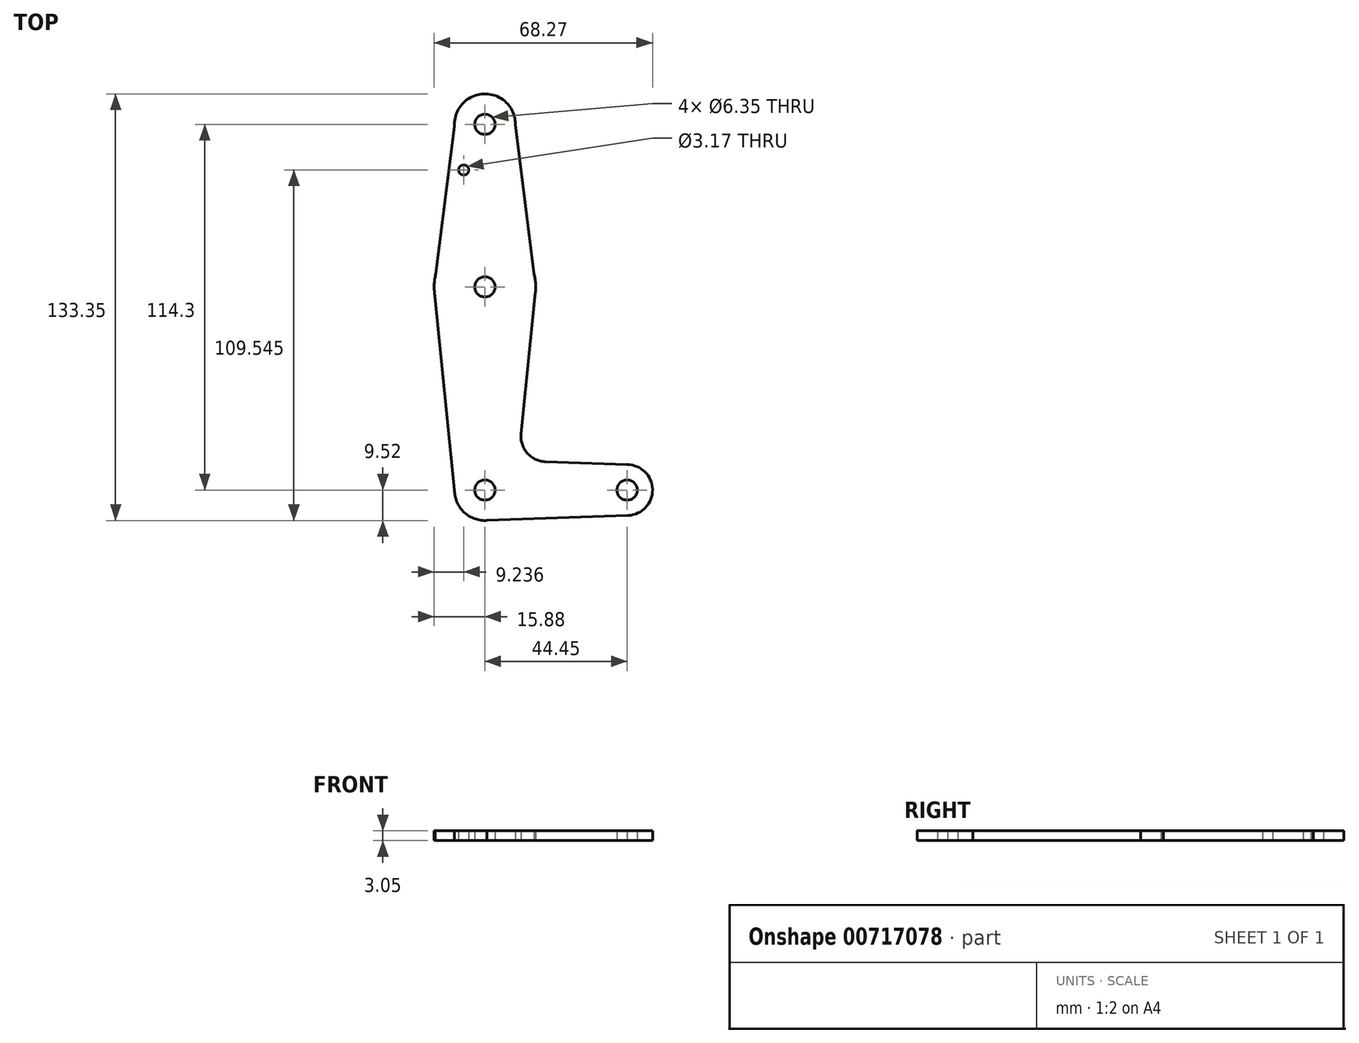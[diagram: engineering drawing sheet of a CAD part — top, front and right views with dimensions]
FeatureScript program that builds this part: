
annotation { "Feature Type Name" : "Feature", "Feature Type Description" : "" }
export const myFeature = defineFeature(function(context is Context, id is Id, definition is map)
    precondition{}
    {
        {
            var Q0;
            Q0=qCreatedBy(makeId("Top.planeOp"),FACE);
            var sketch = newSketch(context, id + "F0", { "sketchPlane" : qUnion([Q0])});
            skCircle(sketch, "E0", {"center": v(0, 114.3) * mm, "radius": 9.53 * mm});
            skCircle(sketch, "E1", {"center": v(44.45, 0) * mm, "radius": 7.94 * mm});
            skCircle(sketch, "E2", {"center": v(0, 63.5) * mm, "radius": 15.88 * mm});
            skLineSegment(sketch, "E3", {"start": v(0, 0) * mm, "end": v(0, 63.5) * mm, "construction": true});
            skLineSegment(sketch, "E4", {"start": v(0, 63.5) * mm, "end": v(0, 114.3) * mm, "construction": true});
            skLineSegment(sketch, "E5", {"start": v(0, 0) * mm, "end": v(44.45, 0) * mm, "construction": true});
            skCircle(sketch, "E6", {"center": v(0, 114.3) * mm, "radius": 0.29 * mm});
            skCircle(sketch, "E7", {"center": v(0, 0) * mm, "radius": 0.29 * mm});
            skCircle(sketch, "E8", {"center": v(44.45, 0) * mm, "radius": 0.29 * mm});
            skCircle(sketch, "E9", {"center": v(0, 63.5) * mm, "radius": 0.29 * mm});
            skCircle(sketch, "E10", {"center": v(0, 0) * mm, "radius": 9.53 * mm});
            skLineSegment(sketch, "E11", {"start": v(-9.5, 113.6) * mm, "end": v(-15.87, 63.45) * mm});
            skLineSegment(sketch, "E12", {"start": v(9.52, 114.3) * mm, "end": v(15.87, 63.45) * mm});
            skLineSegment(sketch, "E13", {"start": v(0, -9.52) * mm, "end": v(44.73, -7.93) * mm});
            skLineSegment(sketch, "E14", {"start": v(18.91, 8.85) * mm, "end": v(44.45, 7.94) * mm});
            skLineSegment(sketch, "E15", {"start": v(11.28, 17.59) * mm, "end": v(15.87, 63.45) * mm});
            skLineSegment(sketch, "E16", {"start": v(-9.53, 0) * mm, "end": v(-15.87, 63.45) * mm});
            skPoint(sketch, "E17.newPointA", {"position": v(9.53, 0) * mm});
            skArc(sketch, "E17.filletArc", {"start": v(11.28, 17.59) * mm, "mid": v(13.2, 11.57) * mm, "end": v(18.91, 8.85) * mm});
            skCircle(sketch, "E18", {"center": v(0, 114.3) * mm, "radius": 3.18 * mm});
            skCircle(sketch, "E19", {"center": v(0, 63.5) * mm, "radius": 3.18 * mm});
            skCircle(sketch, "E20", {"center": v(0, 0) * mm, "radius": 3.18 * mm});
            skCircle(sketch, "E21", {"center": v(44.45, 0) * mm, "radius": 3.18 * mm});
            skCircle(sketch, "E22", {"center": v(-6.64, 100.03) * mm, "radius": 1.59 * mm});
            skSolve(sketch);
        }
        {
            var Q0;
            Q0 = qSketchRegion(id + "F0", true);
            extrude(context, id + "F1", {"entities" : qUnion([Q0]), "depth" : 3.05 * mm, "offsetDistance" : 25.4 * mm});
        }
    });
